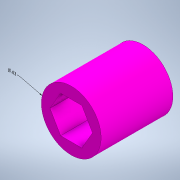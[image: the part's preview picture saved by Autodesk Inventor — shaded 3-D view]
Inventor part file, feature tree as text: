
AUTODESK INVENTOR PART (.ipt)
format: ipt  version: 2022.1 (Build 261234000, 234)  size: 129,024 bytes
history: native  units: in
note: dims shown in document units (in); Inventor stores cm internally (conversion verified against a paired STEP export)
features: other x3, extrude x1, sketch x1
ambient origin geometry x8: Origin, YZ Plane, XZ Plane, XY Plane, X Axis, Y Axis, Z Axis, Center Point
bodies: Solid1 (feature_tree)
feature tree (5):
  other  "Annotations"
  extrude  "Extrusion1"  Depth=0.75in
  other  "Thicken Hex"
  sketch  "Sketch1"  dims[d0=0.375in d2=0.625in d3=0.096in d4=0.75in d5=0.0in d6=0.005in d7=0.005in d8=1.1428in d9=0.625in]
  other  "Diameter Dimension 1"
